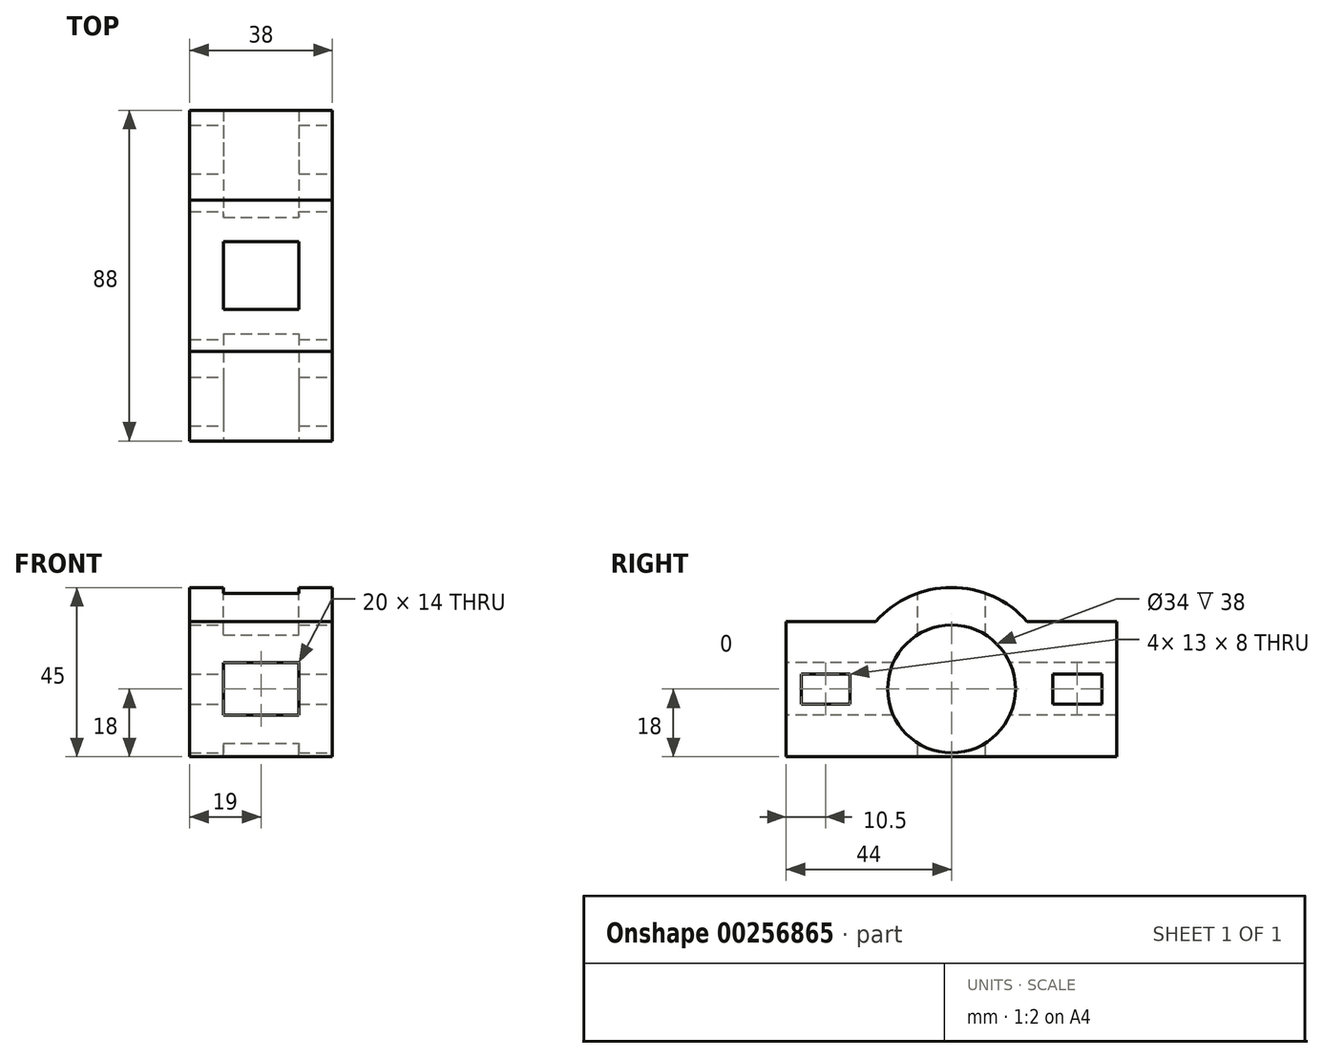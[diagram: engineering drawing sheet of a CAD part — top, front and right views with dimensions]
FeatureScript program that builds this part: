
annotation { "Feature Type Name" : "Feature", "Feature Type Description" : "" }
export const myFeature = defineFeature(function(context is Context, id is Id, definition is map)
    precondition{}
    {
        {
            var Q0;
            Q0=qCreatedBy(makeId("Right.planeOp"),FACE);
            var sketch = newSketch(context, id + "F0", { "sketchPlane" : qUnion([Q0])});
            skCircle(sketch, "E0", {"center": v(0, 0) * mm, "radius": 27 * mm});
            skLineSegment(sketch, "E1.bottom", {"start": v(44, 18) * mm, "end": v(-44, 18) * mm});
            skLineSegment(sketch, "E1.top", {"start": v(44, -18) * mm, "end": v(-44, -18) * mm});
            skLineSegment(sketch, "E1.left", {"start": v(44, 18) * mm, "end": v(44, -18) * mm});
            skLineSegment(sketch, "E1.right", {"start": v(-44, 18) * mm, "end": v(-44, -18) * mm});
            skSolve(sketch);
        }
        {
            var Q0;
            {var subQ0=sQuery(id+"F0.wireOp",EDGE,"E1.bottom");var subQ1=sQuery(id+"F0.wireOp",EDGE,"E0");var subQ2=makeQuery(id+"F0.imprint","INTERSECT",VERTEX,{"disambiguationData":[OD(0.0)],"derivedFrom":[subQ1,subQ0]});Q0=makeQuery(id+"F0.imprint","IMPRINT",FACE,{"disambiguationData":[TD([[makeQuery(id+"F0.imprint","IMPRINT",EDGE,{"disambiguationData":[TD([[subQ2,-1.0]])],"derivedFrom":subQ1}),1.0]])]});}
            var Q1;
            {var subQ5=sQuery(id+"F0.wireOp",EDGE,"E1.right");Q1=makeQuery(id+"F0.imprint","IMPRINT",FACE,{"disambiguationData":[TD([[makeQuery(id+"F0.imprint","IMPRINT",EDGE,{"derivedFrom":subQ5}),1.0]])]});}
            var Q2;
            {var subQ0=sQuery(id+"F0.wireOp",EDGE,"E1.bottom");var subQ1=sQuery(id+"F0.wireOp",EDGE,"E0");var subQ2=makeQuery(id+"F0.imprint","INTERSECT",VERTEX,{"disambiguationData":[OD(0.0)],"derivedFrom":[subQ1,subQ0]});Q2=makeQuery(id+"F0.imprint","IMPRINT",FACE,{"disambiguationData":[TD([[makeQuery(id+"F0.imprint","IMPRINT",EDGE,{"disambiguationData":[TD([[subQ2,1.0]])],"derivedFrom":subQ1}),1.0]])]});}
            var Q3;
            {var subQ5=sQuery(id+"F0.wireOp",EDGE,"E1.left");Q3=makeQuery(id+"F0.imprint","IMPRINT",FACE,{"disambiguationData":[TD([[makeQuery(id+"F0.imprint","IMPRINT",EDGE,{"derivedFrom":subQ5}),-1.0]])]});}
            var Q4;
            {var subQ0=sQuery(id+"F0.wireOp",EDGE,"E1.top");var subQ1=sQuery(id+"F0.wireOp",EDGE,"E0");var subQ2=makeQuery(id+"F0.imprint","INTERSECT",VERTEX,{"disambiguationData":[OD(0.0)],"derivedFrom":[subQ1,subQ0]});Q4=makeQuery(id+"F0.imprint","IMPRINT",FACE,{"disambiguationData":[TD([[makeQuery(id+"F0.imprint","IMPRINT",EDGE,{"disambiguationData":[TD([[subQ2,-1.0]])],"derivedFrom":subQ1}),1.0]])]});}
            extrude(context, id + "F1", {"entities" : qUnion([Q0, Q1, Q2, Q3, Q4]), "endBound" : BoundingType.SYMMETRIC, "depth" : 38 * mm});
        }
        {
            var Q0;
            Q0=makeQuery(id+"F1.opExtrude","CAP_FACE",FACE,{"disambiguationData":[OSD([sQuery(id+"F0.wireOp",EDGE,"E0"),sQuery(id+"F0.wireOp",EDGE,"E1.bottom"),sQuery(id+"F0.wireOp",EDGE,"E1.top"),sQuery(id+"F0.wireOp",EDGE,"E1.left"),sQuery(id+"F0.wireOp",EDGE,"E1.right")])],"isStart":false});
            var sketch = newSketch(context, id + "F2", { "sketchPlane" : qUnion([Q0])});
            skPoint(sketch, "E2", {"position": v(0, 0) * mm});
            skSolve(sketch);
        }
        {
            var Q0;
            Q0=sQuery(id+"F2.wireOp",VERTEX,"E2");
            var Q1;
            Q1=makeQuery(id+"F1.opExtrude","SWEPT_BODY",BODY,{"disambiguationData":[OSD([sQuery(id+"F0.wireOp",EDGE,"E0"),sQuery(id+"F0.wireOp",EDGE,"E1.bottom"),sQuery(id+"F0.wireOp",EDGE,"E1.top"),sQuery(id+"F0.wireOp",EDGE,"E1.left"),sQuery(id+"F0.wireOp",EDGE,"E1.right")])]});
            hole(context, id + "F3", {"style" : HoleStyle.SIMPLE, "endStyle" : HoleEndStyle.THROUGH, "holeDiameter" : 34 * mm, "tappedDepth" : 12 * mm, "tapClearance" : 3, "locations" : qUnion([Q0]), "scope" : qUnion([Q1])});
        }
        {
            var Q0;
            Q0=qCreatedBy(makeId("Top.planeOp"),FACE);
            var sketch = newSketch(context, id + "F4", { "sketchPlane" : qUnion([Q0])});
            skLineSegment(sketch, "E3.bottom", {"start": v(-10, 9) * mm, "end": v(10, 9) * mm});
            skLineSegment(sketch, "E3.top", {"start": v(-10, -9) * mm, "end": v(10, -9) * mm});
            skLineSegment(sketch, "E3.left", {"start": v(-10, 9) * mm, "end": v(-10, -9) * mm});
            skLineSegment(sketch, "E3.right", {"start": v(10, 9) * mm, "end": v(10, -9) * mm});
            skPoint(sketch, "E3.middle", {"position": v(0, 0) * mm});
            skSolve(sketch);
        }
        {
            var Q0;
            Q0=makeQuery(id+"F4.imprint","IMPRINT",FACE,{"disambiguationData":[TD([[makeQuery(id+"F4.imprint","IMPRINT",EDGE,{"derivedFrom":sQuery(id+"F4.wireOp",EDGE,"E3.bottom")}),-1.0]])]});
            extrude(context, id + "F5", {"entities" : qUnion([Q0]), "operationType" : NewBodyOperationType.REMOVE, "endBound" : BoundingType.SYMMETRIC, "oppositeDirection" : true, "depth" : 54 * mm});
        }
        {
            var Q0;
            Q0=qCreatedBy(makeId("Right.planeOp"),FACE);
            var sketch = newSketch(context, id + "F6", { "sketchPlane" : qUnion([Q0])});
            skLineSegment(sketch, "E4.bottom", {"start": v(44, 27) * mm, "end": v(-44, 27) * mm});
            skLineSegment(sketch, "E4.top", {"start": v(44, -27) * mm, "end": v(-44, -27) * mm});
            skLineSegment(sketch, "E4.left", {"start": v(44, 27) * mm, "end": v(44, -27) * mm});
            skLineSegment(sketch, "E4.right", {"start": v(-44, 27) * mm, "end": v(-44, -27) * mm});
            skPoint(sketch, "E4.middle", {"position": v(0, 0) * mm});
            skLineSegment(sketch, "E5", {"start": v(-27, 27) * mm, "end": v(-27, -27) * mm});
            skLineSegment(sketch, "E6", {"start": v(-40, 27) * mm, "end": v(-40, -27) * mm});
            skLineSegment(sketch, "E7", {"start": v(27, 27) * mm, "end": v(27, -27) * mm});
            skLineSegment(sketch, "E8", {"start": v(40, 27) * mm, "end": v(40, -27) * mm});
            skLineSegment(sketch, "E9", {"start": v(-44, 4) * mm, "end": v(44, 4) * mm});
            skLineSegment(sketch, "E10", {"start": v(-44, -4) * mm, "end": v(44, -4) * mm});
            skSolve(sketch);
        }
        {
            var Q0;
            {var subQ0=sQuery(id+"F6.wireOp",EDGE,"E9");var subQ1=sQuery(id+"F6.wireOp",EDGE,"E5");var subQ2=makeQuery(id+"F6.imprint","INTERSECT",VERTEX,{"derivedFrom":[subQ1,subQ0]});Q0=makeQuery(id+"F6.imprint","IMPRINT",FACE,{"disambiguationData":[TD([[makeQuery(id+"F6.imprint","IMPRINT",EDGE,{"disambiguationData":[TD([[subQ2,-1.0]])],"derivedFrom":subQ1}),-1.0]])]});}
            var Q1;
            {var subQ0=sQuery(id+"F6.wireOp",EDGE,"E9");var subQ1=sQuery(id+"F6.wireOp",EDGE,"E7");var subQ2=makeQuery(id+"F6.imprint","INTERSECT",VERTEX,{"derivedFrom":[subQ1,subQ0]});Q1=makeQuery(id+"F6.imprint","IMPRINT",FACE,{"disambiguationData":[TD([[makeQuery(id+"F6.imprint","IMPRINT",EDGE,{"disambiguationData":[TD([[subQ2,-1.0]])],"derivedFrom":subQ1}),1.0]])]});}
            extrude(context, id + "F7", {"entities" : qUnion([Q0, Q1]), "operationType" : NewBodyOperationType.REMOVE, "endBound" : BoundingType.SYMMETRIC, "oppositeDirection" : true, "depth" : 38 * mm});
        }
        {
            var Q0;
            Q0=qCreatedBy(makeId("Front.planeOp"),FACE);
            var sketch = newSketch(context, id + "F8", { "sketchPlane" : qUnion([Q0])});
            skLineSegment(sketch, "E11.bottom", {"start": v(-19, 27) * mm, "end": v(19, 27) * mm});
            skLineSegment(sketch, "E11.top", {"start": v(-19, -27) * mm, "end": v(19, -27) * mm});
            skLineSegment(sketch, "E11.left", {"start": v(-19, 27) * mm, "end": v(-19, -27) * mm});
            skLineSegment(sketch, "E11.right", {"start": v(19, 27) * mm, "end": v(19, -27) * mm});
            skPoint(sketch, "E11.middle", {"position": v(0, 0) * mm});
            skLineSegment(sketch, "E12.bottom", {"start": v(-10, -7) * mm, "end": v(10, -7) * mm});
            skLineSegment(sketch, "E12.top", {"start": v(-10, 7) * mm, "end": v(10, 7) * mm});
            skLineSegment(sketch, "E12.left", {"start": v(-10, -7) * mm, "end": v(-10, 7) * mm});
            skLineSegment(sketch, "E12.right", {"start": v(10, -7) * mm, "end": v(10, 7) * mm});
            skSolve(sketch);
        }
        {
            var Q0;
            Q0=makeQuery(id+"F8.imprint","IMPRINT",FACE,{"disambiguationData":[TD([[makeQuery(id+"F8.imprint","IMPRINT",EDGE,{"derivedFrom":sQuery(id+"F8.wireOp",EDGE,"E12.bottom")}),1.0]])]});
            extrude(context, id + "F9", {"entities" : qUnion([Q0]), "operationType" : NewBodyOperationType.REMOVE, "endBound" : BoundingType.SYMMETRIC, "oppositeDirection" : true, "depth" : 88 * mm});
        }
    });
